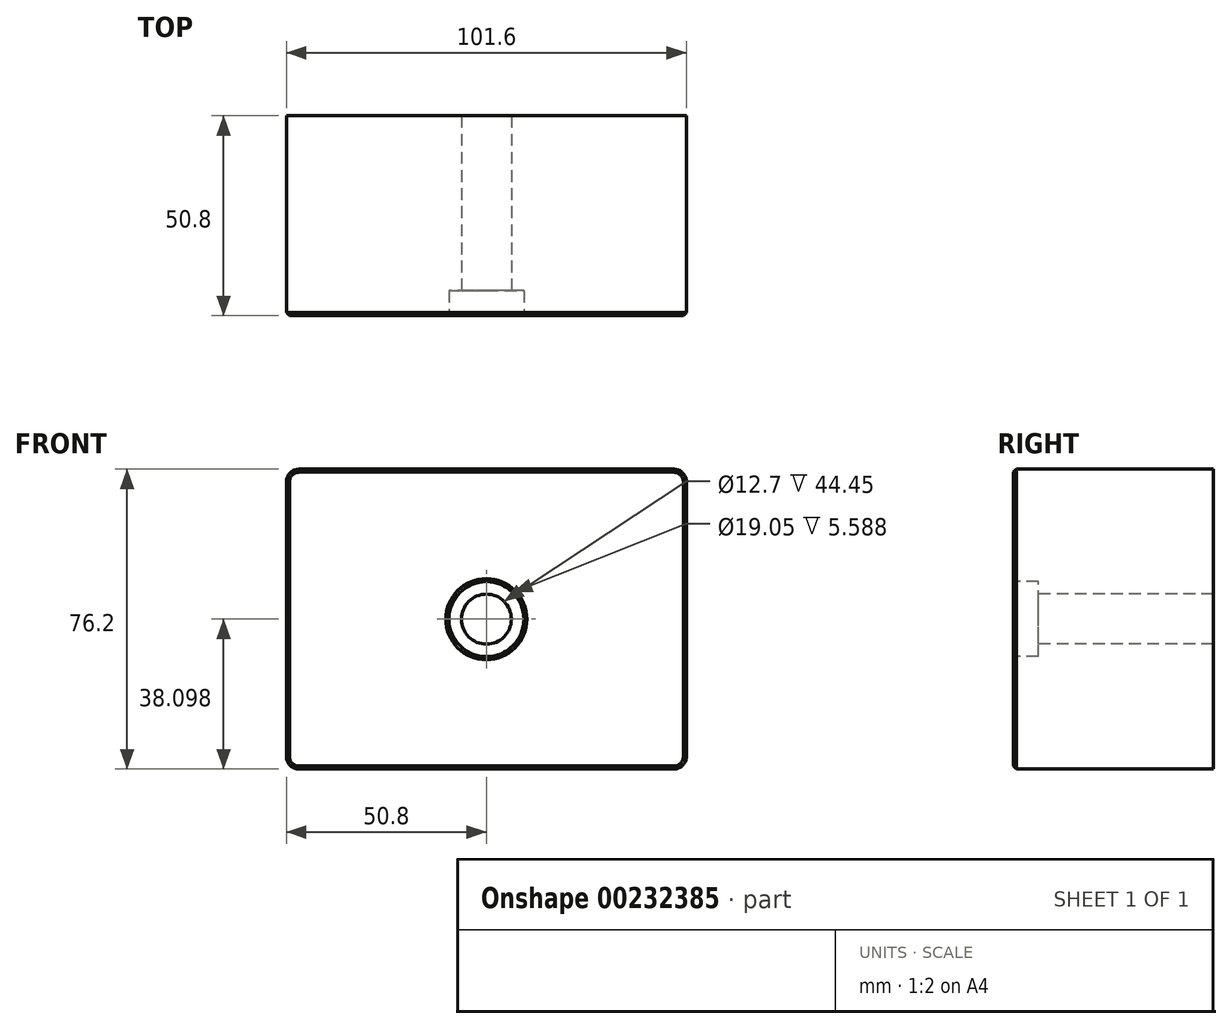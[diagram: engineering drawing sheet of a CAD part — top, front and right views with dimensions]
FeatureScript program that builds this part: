
annotation { "Feature Type Name" : "Feature", "Feature Type Description" : "" }
export const myFeature = defineFeature(function(context is Context, id is Id, definition is map)
    precondition{}
    {
        {
            var Q0;
            Q0=qCreatedBy(makeId("Front.planeOp"),FACE);
            var sketch = newSketch(context, id + "F0", { "sketchPlane" : qUnion([Q0])});
            skLineSegment(sketch, "E0.bottom", {"start": v(-46.65, 36.24) * mm, "end": v(54.95, 36.24) * mm});
            skLineSegment(sketch, "E0.top", {"start": v(-46.65, -39.96) * mm, "end": v(54.95, -39.96) * mm});
            skLineSegment(sketch, "E0.left", {"start": v(-46.65, 36.24) * mm, "end": v(-46.65, -39.96) * mm});
            skLineSegment(sketch, "E0.right", {"start": v(54.95, 36.24) * mm, "end": v(54.95, -39.96) * mm});
            skSolve(sketch);
        }
        {
            var Q0;
            Q0=makeQuery(id+"F0.imprint","IMPRINT",FACE,{"disambiguationData":[TD([[makeQuery(id+"F0.imprint","IMPRINT",EDGE,{"derivedFrom":sQuery(id+"F0.wireOp",EDGE,"E0.bottom")}),-1.0]])]});
            extrude(context, id + "F1", {"entities" : qUnion([Q0]), "oppositeDirection" : true, "depth" : 50.8 * mm});
        }
        {
            var Q0;
            Q0=makeQuery(id+"F1.opExtrude","CAP_FACE",FACE,{"disambiguationData":[OSD([sQuery(id+"F0.wireOp",EDGE,"E0.bottom"),sQuery(id+"F0.wireOp",EDGE,"E0.top"),sQuery(id+"F0.wireOp",EDGE,"E0.left"),sQuery(id+"F0.wireOp",EDGE,"E0.right")])],"isStart":true});
            var sketch = newSketch(context, id + "F2", { "sketchPlane" : qUnion([Q0])});
            skPoint(sketch, "E1", {"position": v(4.15, -1.86) * mm});
            skSolve(sketch);
        }
        {
            var Q0;
            Q0=sQuery(id+"F2.wireOp",VERTEX,"E1");
            var Q1;
            Q1=makeQuery(id+"F1.opExtrude","SWEPT_BODY",BODY,{"disambiguationData":[OSD([sQuery(id+"F0.wireOp",EDGE,"E0.bottom"),sQuery(id+"F0.wireOp",EDGE,"E0.top"),sQuery(id+"F0.wireOp",EDGE,"E0.left"),sQuery(id+"F0.wireOp",EDGE,"E0.right")])]});
            hole(context, id + "F3", {"style" : HoleStyle.C_BORE, "endStyle" : HoleEndStyle.THROUGH, "holeDiameter" : 12.7 * mm, "cBoreDiameter" : 19.05 * mm, "cBoreDepth" : 6.35 * mm, "locations" : qUnion([Q0]), "scope" : qUnion([Q1]), "isTappedThrough" : true});
        }
        {
            var Q0;
            Q0=makeQuery(id+"F1.opExtrude","SWEPT_EDGE",EDGE,{"disambiguationData":[OSD([sQuery(id+"F0.wireOp",EDGE,"E0.bottom"),sQuery(id+"F0.wireOp",EDGE,"E0.right")])]});
            var Q1;
            Q1=makeQuery(id+"F1.opExtrude","SWEPT_EDGE",EDGE,{"disambiguationData":[OSD([sQuery(id+"F0.wireOp",EDGE,"E0.bottom"),sQuery(id+"F0.wireOp",EDGE,"E0.left")])]});
            var Q2;
            Q2=makeQuery(id+"F1.opExtrude","SWEPT_EDGE",EDGE,{"disambiguationData":[OSD([sQuery(id+"F0.wireOp",EDGE,"E0.top"),sQuery(id+"F0.wireOp",EDGE,"E0.right")])]});
            var Q3;
            Q3=makeQuery(id+"F1.opExtrude","SWEPT_EDGE",EDGE,{"disambiguationData":[OSD([sQuery(id+"F0.wireOp",EDGE,"E0.top"),sQuery(id+"F0.wireOp",EDGE,"E0.left")])]});
            fillet(context, id + "F4", {"entities" : qUnion([Q0, Q1, Q2, Q3]), "radius" : 3.17 * mm, "tangentPropagation" : true, "allowEdgeOverflow" : false});
        }
        {
            var Q0;
            Q0=makeQuery(id+"F1.opExtrude","CAP_FACE",FACE,{"disambiguationData":[OSD([sQuery(id+"F0.wireOp",EDGE,"E0.bottom"),sQuery(id+"F0.wireOp",EDGE,"E0.top"),sQuery(id+"F0.wireOp",EDGE,"E0.left"),sQuery(id+"F0.wireOp",EDGE,"E0.right")])],"isStart":true});
            chamfer(context, id + "F5", {"entities" : qUnion([Q0]), "width" : 0.76 * mm, "tangentPropagation" : true});
        }
    });
